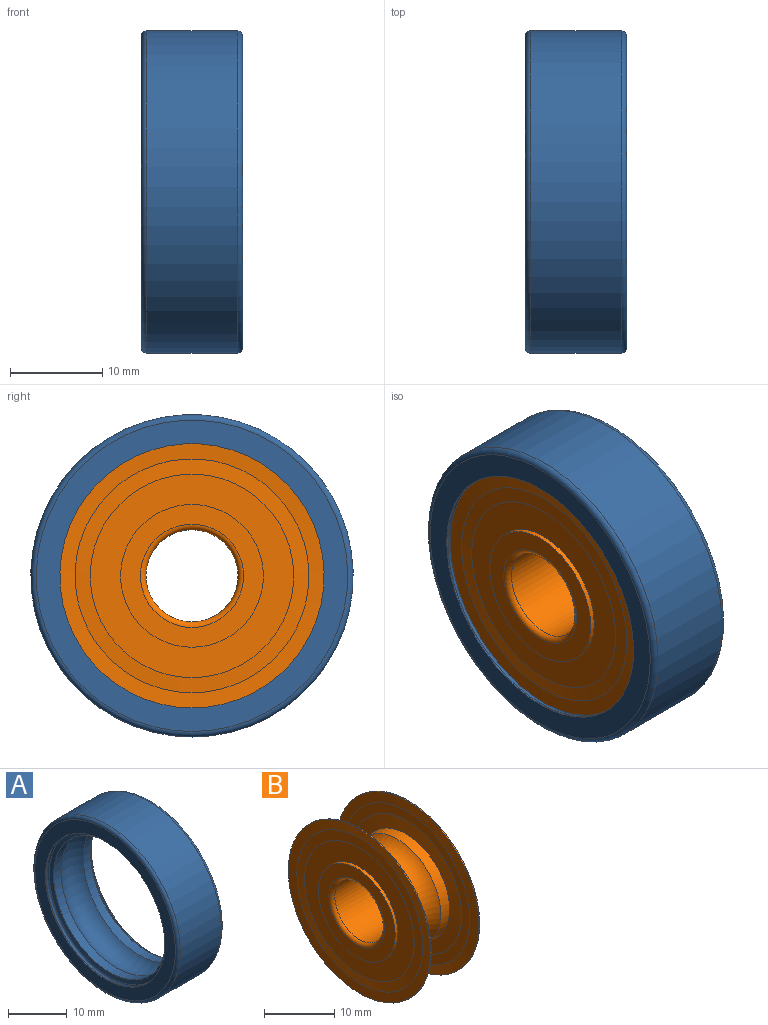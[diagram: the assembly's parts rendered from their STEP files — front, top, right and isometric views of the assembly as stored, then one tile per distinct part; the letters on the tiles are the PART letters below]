
ASSEMBLY  parts=2 mates=1
PART A: 14 faces, bbox 11x37.9x37.9 mm
  f0: plane 33.8x33.8mm, normal (-1,0,0), area 251.2mm2, adj f1,f13
  f1: cylinder r=14.34mm len=28.68mm, axis (-1,0,0), area 16.2mm2, adj f0,f2
  f2: torus R=14.34mm, axis (1,0,0), area 103.5mm2, adj f1,f3
  f3: cone r=14.34mm half-angle=80deg, axis (-1,0,0), area 78.9mm2, adj f2,f4
  f4: cylinder r=13.45mm len=26.9mm, axis (-1,0,0), area 148.1mm2, adj f3,f5
  f5: torus R=11.1mm, axis (1,0,0), area 545.6mm2, adj f4,f6
  f6: cylinder r=13.45mm len=26.9mm, axis (-1,0,0), area 148.1mm2, adj f5,f7
  f7: cone r=13.45mm half-angle=80deg, axis (1,0,0), area 78.9mm2, adj f6,f8
  f8: torus R=14.34mm, axis (1,0,0), area 103.5mm2, adj f7,f9
  f9: cylinder r=14.34mm len=28.68mm, axis (-1,0,0), area 16.2mm2, adj f8,f10
  f10: plane 33.8x33.8mm, normal (1,0,0), area 251.2mm2, adj f9,f11
  f11: torus R=16.9mm, axis (1,0,0), area 102.3mm2, adj f10,f12
  f12: cylinder r=17.5mm len=35mm, axis (-1,0,0), area 1077.6mm2, adj f11,f13
  f13: torus R=16.9mm, axis (1,0,0), area 102.3mm2, adj f0,f12
PART B: 28 faces, bbox 11x28.7x28.7 mm
  f0: cone r=14.34mm half-angle=83.8deg, axis (1,0,0), area 140.7mm2, adj f1,f27
  f1: plane 25.39x25.39mm, normal (-1,0,0), area 122.9mm2, adj f0,f2
  f2: cone r=11.04mm half-angle=86.9deg, axis (-1,0,0), area 193.6mm2, adj f1,f15
  f3: plane 15.5x15.5mm, normal (-1,0,0), area 90.2mm2, adj f5,f12
  f4: plane 15.5x15.5mm, normal (1,0,0), area 90.2mm2, adj f7,f13
  f5: cylinder r=7.75mm len=15.5mm, axis (-1,0,0), area 26.3mm2, adj f3,f20
  f6: torus R=8.2mm, axis (1,0,0), area 27.6mm2, adj f16,f21
  f7: torus R=5.6mm, axis (1,0,0), area 30.9mm2, adj f4,f11
  f8: cylinder r=8.75mm len=17.5mm, axis (-1,0,0), area 98.4mm2, adj f9,f16
  f9: torus R=11.1mm, axis (1,0,0), area 304.1mm2, adj f8,f10
  f10: cylinder r=8.75mm len=17.5mm, axis (-1,0,0), area 98.4mm2, adj f9,f14
  f11: cylinder r=5mm len=10mm, axis (-1,0,0), area 307.9mm2, adj f7,f12
  f12: torus R=5.6mm, axis (1,0,0), area 30.9mm2, adj f3,f11
  f13: cylinder r=7.75mm len=15.5mm, axis (-1,0,0), area 26.3mm2, adj f4,f24
  f14: plane 17.5x17.5mm, normal (1,0,0), area 29.3mm2, adj f10,f15
  f15: torus R=8.2mm, axis (1,0,0), area 27.6mm2, adj f2,f14
  f16: plane 17.5x17.5mm, normal (-1,0,0), area 29.3mm2, adj f6,f8
  f17: cylinder r=14.34mm len=28.68mm, axis (-1,0,0), area 16.2mm2, adj f18,f23
  f18: cone r=14.34mm half-angle=86.9deg, axis (-1,0,0), area 140.1mm2, adj f17,f19
  f19: cone r=12.69mm half-angle=86.9deg, axis (1,0,0), area 123mm2, adj f18,f20
  f20: plane 22.09x22.09mm, normal (-1,0,0), area 194.6mm2, adj f5,f19
  f21: cone r=7.75mm half-angle=86.9deg, axis (1,0,0), area 193.6mm2, adj f6,f22
  f22: plane 25.39x25.39mm, normal (1,0,0), area 122.9mm2, adj f21,f23
  f23: cone r=12.69mm half-angle=83.8deg, axis (-1,0,0), area 140.7mm2, adj f17,f22
  f24: plane 22.09x22.09mm, normal (1,0,0), area 194.6mm2, adj f13,f25
  f25: cone r=11.04mm half-angle=86.9deg, axis (-1,0,0), area 123mm2, adj f24,f26
  f26: cone r=12.69mm half-angle=86.9deg, axis (1,0,0), area 140.1mm2, adj f25,f27
  f27: cylinder r=14.34mm len=28.68mm, axis (-1,0,0), area 16.2mm2, adj f0,f26
PLACE A t=(-2.24,0.23,2.29)mm
PLACE B t=(-2.24,0.23,2.29)mm
MATE fastened B.f0 <-> A.f1  axis (-1,0,0) through (3.26,0.23,2.29)mm
